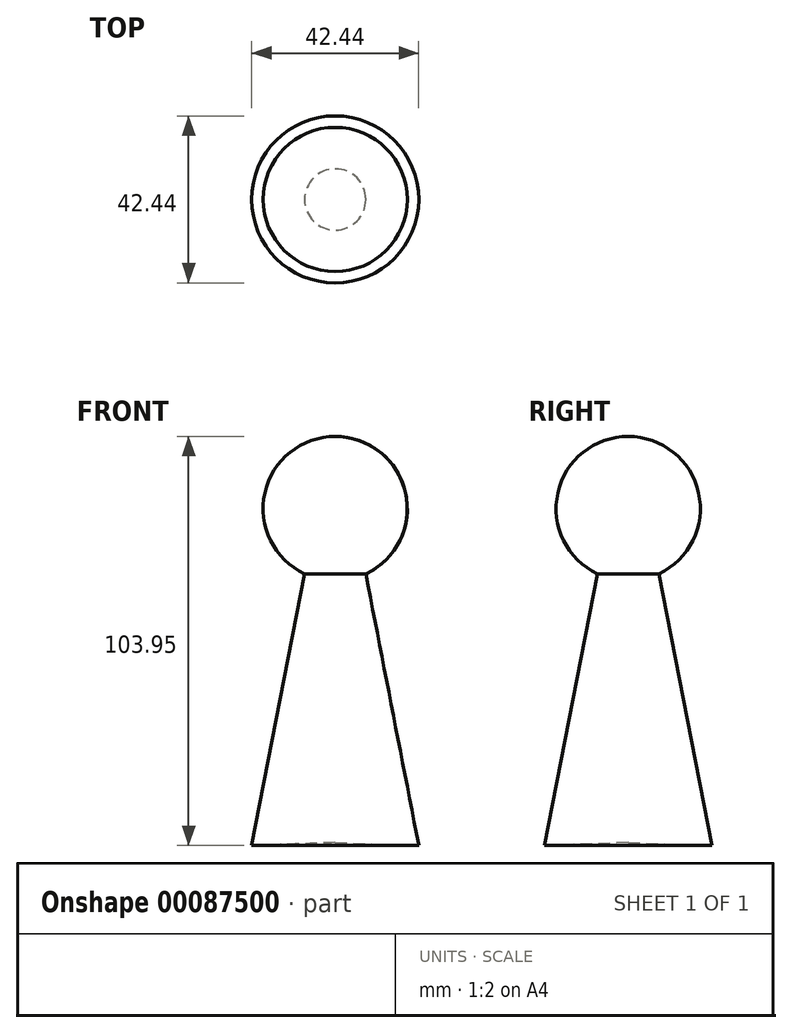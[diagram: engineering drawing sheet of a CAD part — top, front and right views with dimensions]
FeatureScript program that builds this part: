
annotation { "Feature Type Name" : "Feature", "Feature Type Description" : "" }
export const myFeature = defineFeature(function(context is Context, id is Id, definition is map)
    precondition{}
    {
        {
            var Q0;
            Q0=qCreatedBy(makeId("Front.planeOp"),FACE);
            var sketch = newSketch(context, id + "F0", { "sketchPlane" : qUnion([Q0])});
            skArc(sketch, "E0", {"start": v(7.78, 24.42) * mm, "mid": v(17.88, 44.98) * mm, "end": v(0, 59.32) * mm});
            skLineSegment(sketch, "E1", {"start": v(0, 22.69) * mm, "end": v(0, 59.32) * mm});
            skLineSegment(sketch, "E2", {"start": v(0, 22.69) * mm, "end": v(0, -43.88) * mm});
            skLineSegment(sketch, "E3", {"start": v(7.78, 24.42) * mm, "end": v(21.22, -44.63) * mm});
            skLineSegment(sketch, "E4", {"start": v(21.22, -44.63) * mm, "end": v(0, -43.88) * mm});
            skSolve(sketch);
        }
        {
            var Q0;
            Q0=makeQuery(id+"F0.imprint","IMPRINT",FACE,{"disambiguationData":[TD([[makeQuery(id+"F0.imprint","IMPRINT",EDGE,{"derivedFrom":sQuery(id+"F0.wireOp",EDGE,"E0")}),1.0]])]});
            var Q1;
            Q1 = qSketchRegion(id + "F2", true);
            var Q2;
            Q2=sQuery(id+"F0.wireOp",EDGE,"E2");
            revolve(context, id + "F1", {"entities" : qUnion([Q0, Q1]), "axis" : qUnion([Q2]), "revolveType" : RevolveType.FULL});
        }
    });
